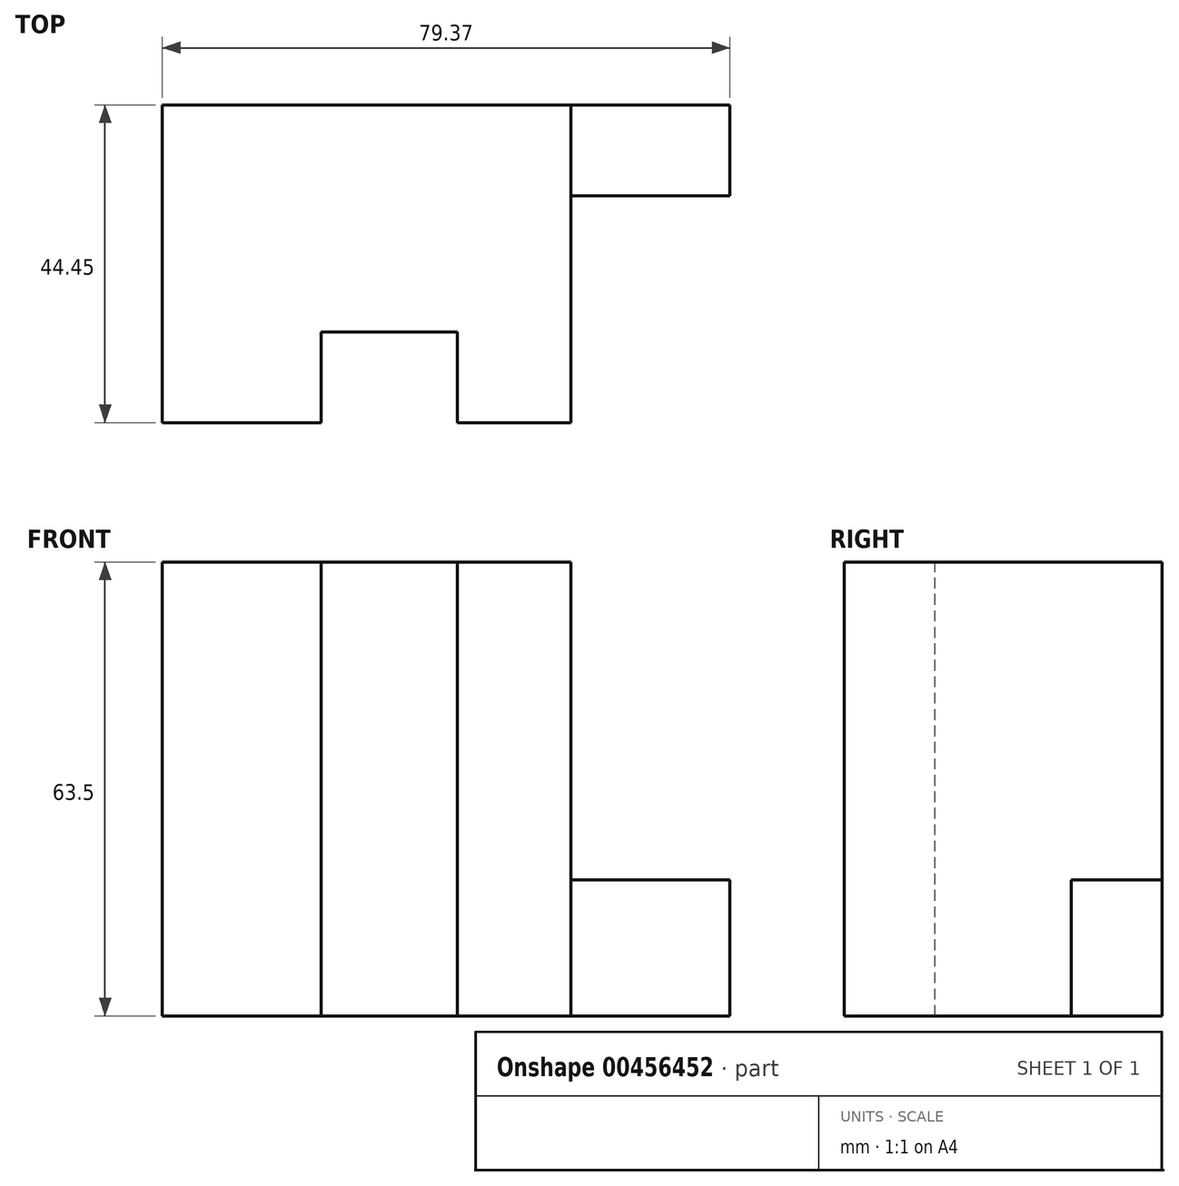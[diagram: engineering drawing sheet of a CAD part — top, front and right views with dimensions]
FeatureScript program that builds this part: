
annotation { "Feature Type Name" : "Feature", "Feature Type Description" : "" }
export const myFeature = defineFeature(function(context is Context, id is Id, definition is map)
    precondition{}
    {
        {
            var Q0;
            Q0=qCreatedBy(makeId("Front.planeOp"),FACE);
            var sketch = newSketch(context, id + "F0", { "sketchPlane" : qUnion([Q0])});
            skLineSegment(sketch, "E0.bottom", {"start": v(-28.57, -31.75) * mm, "end": v(28.58, -31.75) * mm});
            skLineSegment(sketch, "E0.top", {"start": v(-28.58, 31.75) * mm, "end": v(28.57, 31.75) * mm});
            skLineSegment(sketch, "E0.left", {"start": v(-28.57, -31.75) * mm, "end": v(-28.58, 31.75) * mm});
            skLineSegment(sketch, "E0.right", {"start": v(28.58, -31.75) * mm, "end": v(28.57, 31.75) * mm});
            skPoint(sketch, "E0.middle", {"position": v(0, 0) * mm});
            skSolve(sketch);
        }
        {
            var Q0;
            Q0 = qSketchRegion(id + "F0", true);
            extrude(context, id + "F1", {"entities" : qUnion([Q0]), "depth" : 44.45 * mm});
        }
        {
            var Q0;
            Q0=makeQuery(id+"F1.opExtrude","CAP_FACE",FACE,{"disambiguationData":[OSD([sQuery(id+"F0.wireOp",EDGE,"E0.bottom"),sQuery(id+"F0.wireOp",EDGE,"E0.top"),sQuery(id+"F0.wireOp",EDGE,"E0.left"),sQuery(id+"F0.wireOp",EDGE,"E0.right")])],"isStart":true});
            var sketch = newSketch(context, id + "F2", { "sketchPlane" : qUnion([Q0])});
            skLineSegment(sketch, "E1.bottom", {"start": v(-28.58, -31.75) * mm, "end": v(-50.8, -31.75) * mm});
            skLineSegment(sketch, "E1.top", {"start": v(-28.58, -12.7) * mm, "end": v(-50.8, -12.7) * mm});
            skLineSegment(sketch, "E1.left", {"start": v(-28.58, -31.75) * mm, "end": v(-28.58, -12.7) * mm});
            skLineSegment(sketch, "E1.right", {"start": v(-50.8, -31.75) * mm, "end": v(-50.8, -12.7) * mm});
            skSolve(sketch);
        }
        {
            var Q0;
            Q0 = qSketchRegion(id + "F2", true);
            extrude(context, id + "F3", {"entities" : qUnion([Q0]), "operationType" : NewBodyOperationType.ADD, "oppositeDirection" : true, "depth" : 12.7 * mm});
        }
        {
            var Q0;
            Q0=makeQuery(id+"F1.opExtrude","SWEPT_FACE",FACE,{"disambiguationData":[OSD([sQuery(id+"F0.wireOp",EDGE,"E0.top")])]});
            var sketch = newSketch(context, id + "F4", { "sketchPlane" : qUnion([Q0])});
            skLineSegment(sketch, "E2.bottom", {"start": v(-6.35, -44.45) * mm, "end": v(12.7, -44.45) * mm});
            skLineSegment(sketch, "E2.top", {"start": v(-6.35, -31.75) * mm, "end": v(12.7, -31.75) * mm});
            skLineSegment(sketch, "E2.left", {"start": v(-6.35, -44.45) * mm, "end": v(-6.35, -31.75) * mm});
            skLineSegment(sketch, "E2.right", {"start": v(12.7, -44.45) * mm, "end": v(12.7, -31.75) * mm});
            skSolve(sketch);
        }
        {
            var Q0;
            Q0=makeQuery(id+"F4.imprint","IMPRINT",FACE,{"disambiguationData":[TD([[makeQuery(id+"F4.imprint","IMPRINT",EDGE,{"derivedFrom":sQuery(id+"F4.wireOp",EDGE,"E2.bottom")}),1.0]])]});
            extrude(context, id + "F5", {"entities" : qUnion([Q0]), "operationType" : NewBodyOperationType.REMOVE, "endBound" : BoundingType.THROUGH_ALL, "oppositeDirection" : true, "depth" : 25.4 * mm});
        }
    });
